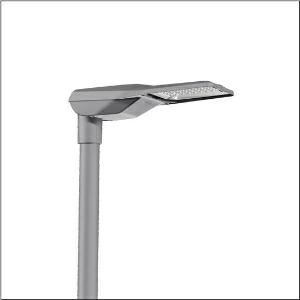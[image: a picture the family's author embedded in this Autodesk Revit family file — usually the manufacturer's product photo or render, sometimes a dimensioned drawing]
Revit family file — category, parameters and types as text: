
# Revit family: streetlight_sl_21_iq_mini___st1_0a_5xe2d61g08hb_24ab
name_source: partatom
category: Lighting Fixtures
units: mm (PartAtom-declared; Revit-internal decimal feet)

## family parameters
Cut with Voids When Loaded = No
Host = Face
Light Source = No
Part Type = Normal
Room Calculation Point = No
Round Connector Dimension = Use Diameter
Shared = No

## types (1)
- --- (1 x LED, 8480 lm, 70.9 W, 2700K)
    Apparent Load = 71 VA
    CIE Flux Codes = 37 72 97 100 100
    Color Rendering = 70
    Color Temperature = 2700K
    Default Elevation = 1800 mm
    Description = Streetlight SL 21 iQ mini, mast luminaire, primary light control with lens, of PMMA, primary optical cover: cover, of toughened safety glass, transparent, light distribution: ST1.0a, light emission: direct distribution, primary light characteristic: asymmetric, installation type: post-top, side-entry, LED, High Power LED, rated luminous flux: 8.480lm, luminous efficacy: 120lm/W, light colour: 727, colour temperature: 2700K, control: Street-Remote, Auto-Match, Temp-Guard, Lumen-Switch, Night-Set, Smart-Wire, Light-Fading, Desk-Remote (wireless, voltage-free reading and setting of iQ features in the workshop via application-optimized NFC function/RFID function), optimised constant luminous flux control (CLO 2.0), presetting dimming linear, mains connection: 220..240V, AC, 50/60Hz, start of lifetime: 71W, end of service life: 75W, reduction: 31W, luminaire housing, of diecast aluminium, powder-coated, Siteco® metallic grey (DB 702S), corrosivity category C5 mid according to DIN EN ISO 12944, please order mast flange separately, inclination adjustable: 0°, 5°, 10°, 15°, sealing non-destructively replaceable, multi-level sealing system, length: 628mm, width: 235mm, height: 110mm, mast flange for spigot size: 42mm (side-entry): 5XC10008XM4, 60/48mm (side-entry/post-top): 5XC10108XM2, 76/60mm (side-entry/post-top): 5XC10108XM1, protection rating (complete): IP66, insulation class (complete): insulation class II (safety insulation), certification: CE, ENEC, ENEC+, VDE, impact resistance: IK09, permissible operating ambient temperature for outdoor applications: -40..+50°C, standard-compliant lighting for roads and squares, packaging unit: 1 piece

Light Distribution: ST1.0a
    Height = 110 mm
    Lamp = 1 x LED
    Lamp Light Flux = 8480 lm
    Lamp Power = 70.9 W
    Lamp count = 1
    Length = 625 mm
    Luminous efficacy = 120 lm/W
    Manufacturer = Siteco
    ModVariant = No
    Model = 5XE2D61G08HB
    Number of Poles = 1
    OnlyDefault = Yes
    Power Factor = 1
    Product Name = Streetlight SL 21 iQ mini | ST1.0a
    Product group = mast luminaire | pylon top
    ProductGroupID = 6100
    Protection Class = Protection class II
    Protection Degree = IP 66
    RLX_Detail_Level = 1
    RLX_Emergency_Light_Flux = 0 lm
    RLX_Emergency_Type = 0
    RLX_Emergency_Type_DB = No
    RlxData = <blob elided: 92165 chars, md5=7cbb09ab>
    Socket = socket
    Standby Power = 0 W
    System Light Flux = 8480 lm
    System Power = 71 W
    Type Comments = factory setting: luminous flux: 100 % | dim-lin: 254 | 711 mA
    Type Image = l_1003519.jpg
    URL = http://relux.com
    VarID = @adj_108385
    Voltage = 0 V
    Weight = 0.00 kg
    Width = 234 mm

## geometry (parser evidence)
native form markers: Blend x4, Sweep x11
no freeform markers — native parametric forms only
